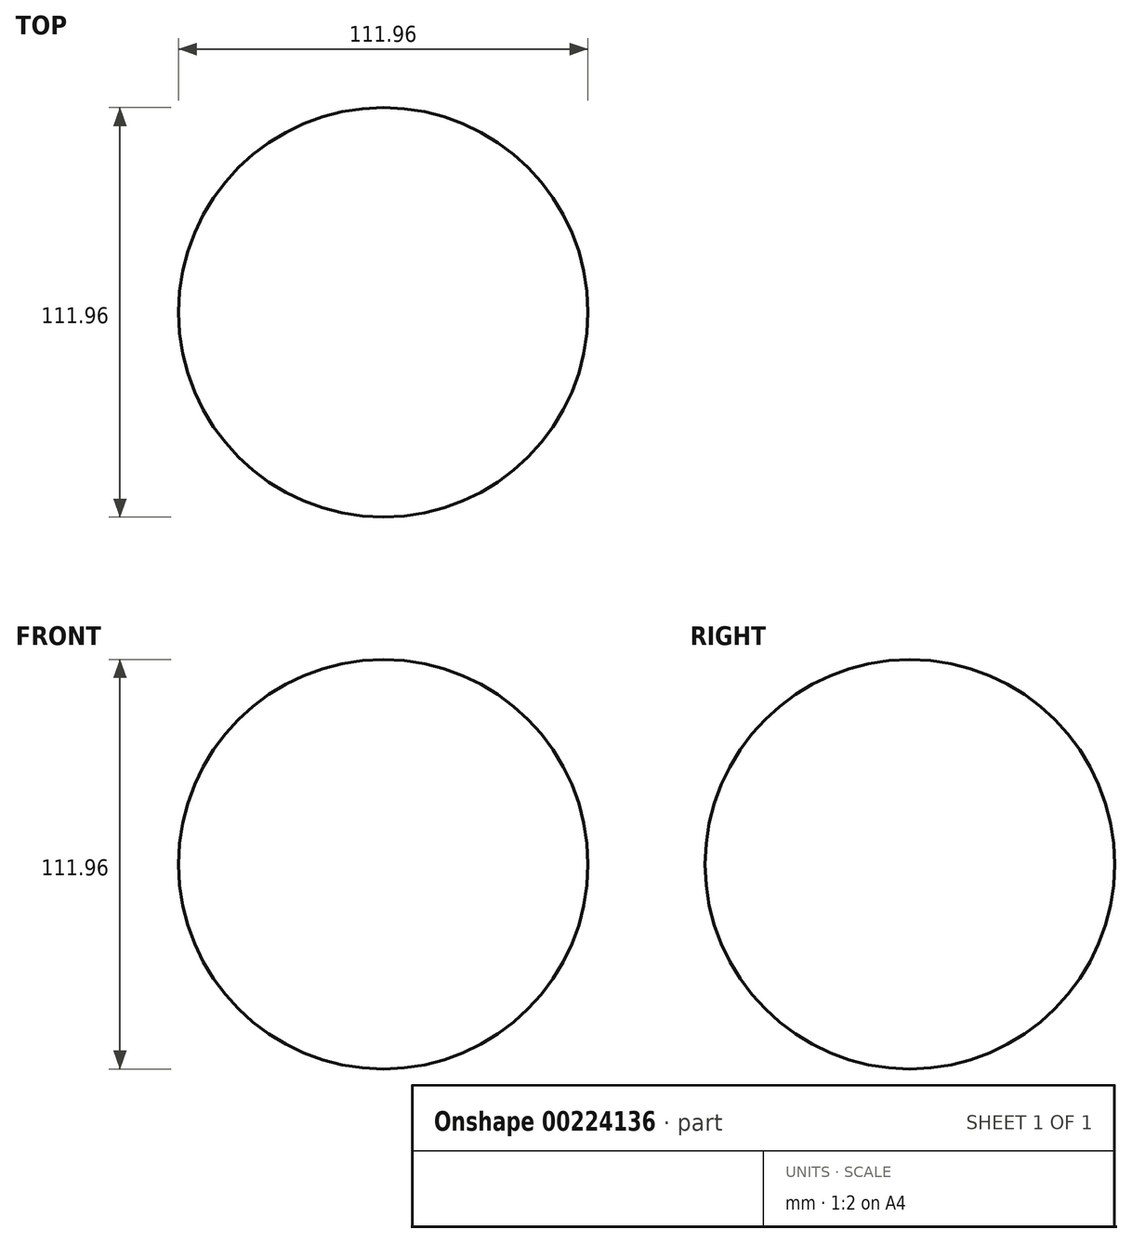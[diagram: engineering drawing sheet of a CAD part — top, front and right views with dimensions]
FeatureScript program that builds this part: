
annotation { "Feature Type Name" : "Feature", "Feature Type Description" : "" }
export const myFeature = defineFeature(function(context is Context, id is Id, definition is map)
    precondition{}
    {
        {
            var Q0;
            Q0=qCreatedBy(makeId("Front.planeOp"),FACE);
            var sketch = newSketch(context, id + "F0", { "sketchPlane" : qUnion([Q0])});
            skCircle(sketch, "E0", {"center": v(0, 0) * mm, "radius": 55.98 * mm});
            skLineSegment(sketch, "E1", {"start": v(0, 55.98) * mm, "end": v(0, 0) * mm});
            skLineSegment(sketch, "E2", {"start": v(0, 0) * mm, "end": v(0, -55.98) * mm});
            skSolve(sketch);
        }
        {
            var Q0;
            {var subQ0=sQuery(id+"F0.wireOp",EDGE,"E1");Q0=makeQuery(id+"F0.imprint","IMPRINT",FACE,{"disambiguationData":[TD([[makeQuery(id+"F0.imprint","IMPRINT",EDGE,{"derivedFrom":subQ0}),1.0]])]});}
            var Q1;
            Q1=sQuery(id+"F0.wireOp",EDGE,"E2");
            revolve(context, id + "F1", {"entities" : qUnion([Q0]), "axis" : qUnion([Q1]), "revolveType" : RevolveType.FULL});
        }
    });
